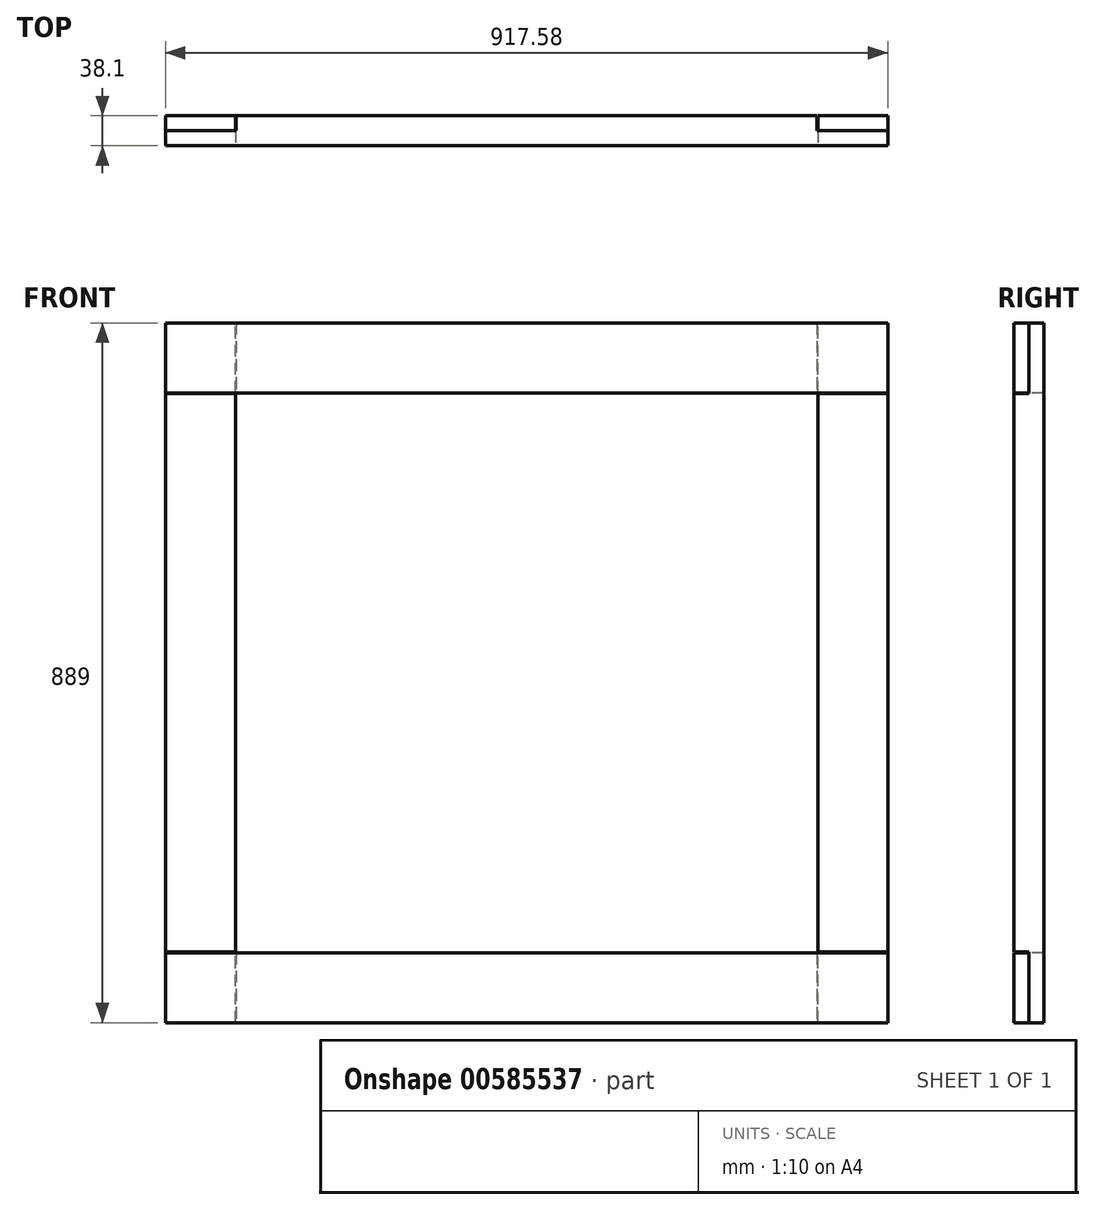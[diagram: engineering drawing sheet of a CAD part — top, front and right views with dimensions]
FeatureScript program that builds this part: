
annotation { "Feature Type Name" : "Feature", "Feature Type Description" : "" }
export const myFeature = defineFeature(function(context is Context, id is Id, definition is map)
    precondition{}
    {
        {
            var Q0;
            Q0=qCreatedBy(makeId("Front.planeOp"),FACE);
            var sketch = newSketch(context, id + "F0", { "sketchPlane" : qUnion([Q0])});
            skLineSegment(sketch, "E0.bottom", {"start": v(0, 0) * mm, "end": v(88.9, 0) * mm});
            skLineSegment(sketch, "E0.top", {"start": v(0, 889) * mm, "end": v(88.9, 889) * mm});
            skLineSegment(sketch, "E0.left", {"start": v(0, 0) * mm, "end": v(0, 889) * mm});
            skLineSegment(sketch, "E0.right", {"start": v(88.9, 0) * mm, "end": v(88.9, 889) * mm});
            skSolve(sketch);
        }
        {
            var Q0;
            Q0 = qSketchRegion(id + "F0", true);
            extrude(context, id + "F1", {"entities" : qUnion([Q0]), "oppositeDirection" : true, "depth" : 38.1 * mm, "offsetDistance" : 25.4 * mm});
        }
        {
            var Q0;
            Q0=makeQuery(id+"F1.opExtrude","CAP_FACE",FACE,{"disambiguationData":[OSD([sQuery(id+"F0.wireOp",EDGE,"E0.bottom"),sQuery(id+"F0.wireOp",EDGE,"E0.top"),sQuery(id+"F0.wireOp",EDGE,"E0.left"),sQuery(id+"F0.wireOp",EDGE,"E0.right")])],"isStart":true});
            var sketch = newSketch(context, id + "F2", { "sketchPlane" : qUnion([Q0])});
            skLineSegment(sketch, "E1.bottom", {"start": v(0, 889) * mm, "end": v(88.9, 889) * mm});
            skLineSegment(sketch, "E1.top", {"start": v(0, 799.31) * mm, "end": v(88.9, 799.31) * mm});
            skLineSegment(sketch, "E1.left", {"start": v(0, 889) * mm, "end": v(0, 799.31) * mm});
            skLineSegment(sketch, "E1.right", {"start": v(88.9, 889) * mm, "end": v(88.9, 799.31) * mm});
            skSolve(sketch);
        }
        {
            var Q0;
            Q0 = qSketchRegion(id + "F2", true);
            extrude(context, id + "F3", {"entities" : qUnion([Q0]), "operationType" : NewBodyOperationType.REMOVE, "oppositeDirection" : true, "depth" : 19.05 * mm, "offsetDistance" : 25.4 * mm});
        }
        {
            var Q0;
            Q0=makeQuery(id+"F1.opExtrude","CAP_FACE",FACE,{"disambiguationData":[OSD([sQuery(id+"F0.wireOp",EDGE,"E0.bottom"),sQuery(id+"F0.wireOp",EDGE,"E0.top"),sQuery(id+"F0.wireOp",EDGE,"E0.left"),sQuery(id+"F0.wireOp",EDGE,"E0.right")])],"isStart":true});
            var sketch = newSketch(context, id + "F4", { "sketchPlane" : qUnion([Q0])});
            skLineSegment(sketch, "E2.bottom", {"start": v(0, 0) * mm, "end": v(88.9, 0) * mm});
            skLineSegment(sketch, "E2.top", {"start": v(0, 89.69) * mm, "end": v(88.9, 89.69) * mm});
            skLineSegment(sketch, "E2.left", {"start": v(0, 0) * mm, "end": v(0, 89.69) * mm});
            skLineSegment(sketch, "E2.right", {"start": v(88.9, 0) * mm, "end": v(88.9, 89.69) * mm});
            skSolve(sketch);
        }
        {
            var Q0;
            Q0 = qSketchRegion(id + "F4", true);
            extrude(context, id + "F5", {"entities" : qUnion([Q0]), "operationType" : NewBodyOperationType.REMOVE, "oppositeDirection" : true, "depth" : 19.05 * mm, "offsetDistance" : 25.4 * mm});
        }
        {
            var Q0;
            Q0=qCreatedBy(makeId("Front.planeOp"),FACE);
            var sketch = newSketch(context, id + "F6", { "sketchPlane" : qUnion([Q0])});
            skLineSegment(sketch, "E3.bottom", {"start": v(828.68, 0) * mm, "end": v(917.58, 0) * mm});
            skLineSegment(sketch, "E3.top", {"start": v(828.68, 889) * mm, "end": v(917.58, 889) * mm});
            skLineSegment(sketch, "E3.left", {"start": v(828.68, 0) * mm, "end": v(828.68, 889) * mm});
            skLineSegment(sketch, "E3.right", {"start": v(917.58, 0) * mm, "end": v(917.58, 889) * mm});
            skSolve(sketch);
        }
        {
            var Q0;
            Q0 = qSketchRegion(id + "F6", true);
            extrude(context, id + "F7", {"entities" : qUnion([Q0]), "oppositeDirection" : true, "depth" : 38.1 * mm, "offsetDistance" : 25.4 * mm});
        }
        {
            var Q0;
            Q0=makeQuery(id+"F7.opExtrude","CAP_FACE",FACE,{"disambiguationData":[OSD([sQuery(id+"F6.wireOp",EDGE,"E3.bottom"),sQuery(id+"F6.wireOp",EDGE,"E3.top"),sQuery(id+"F6.wireOp",EDGE,"E3.left"),sQuery(id+"F6.wireOp",EDGE,"E3.right")])],"isStart":true});
            var sketch = newSketch(context, id + "F8", { "sketchPlane" : qUnion([Q0])});
            skLineSegment(sketch, "E4.bottom", {"start": v(828.68, 889) * mm, "end": v(917.58, 889) * mm});
            skLineSegment(sketch, "E4.top", {"start": v(828.68, 799.31) * mm, "end": v(917.58, 799.31) * mm});
            skLineSegment(sketch, "E4.left", {"start": v(828.68, 889) * mm, "end": v(828.68, 799.31) * mm});
            skLineSegment(sketch, "E4.right", {"start": v(917.58, 889) * mm, "end": v(917.58, 799.31) * mm});
            skLineSegment(sketch, "E5.bottom", {"start": v(917.58, 0) * mm, "end": v(828.68, 0) * mm});
            skLineSegment(sketch, "E5.top", {"start": v(917.58, 89.69) * mm, "end": v(828.68, 89.69) * mm});
            skLineSegment(sketch, "E5.left", {"start": v(917.58, 0) * mm, "end": v(917.58, 89.69) * mm});
            skLineSegment(sketch, "E5.right", {"start": v(828.68, 0) * mm, "end": v(828.68, 89.69) * mm});
            skSolve(sketch);
        }
        {
            var Q0;
            Q0 = qSketchRegion(id + "F8", true);
            extrude(context, id + "F9", {"entities" : qUnion([Q0]), "operationType" : NewBodyOperationType.REMOVE, "oppositeDirection" : true, "depth" : 19.05 * mm, "offsetDistance" : 25.4 * mm});
        }
        {
            var Q0;
            Q0=qCreatedBy(makeId("Front.planeOp"),FACE);
            var sketch = newSketch(context, id + "F10", { "sketchPlane" : qUnion([Q0])});
            skLineSegment(sketch, "E6.bottom", {"start": v(0, 889) * mm, "end": v(917.58, 889) * mm});
            skLineSegment(sketch, "E6.top", {"start": v(0, 800.1) * mm, "end": v(917.58, 800.1) * mm});
            skLineSegment(sketch, "E6.left", {"start": v(0, 889) * mm, "end": v(0, 800.1) * mm});
            skLineSegment(sketch, "E6.right", {"start": v(917.58, 889) * mm, "end": v(917.58, 800.1) * mm});
            skSolve(sketch);
        }
        {
            var Q0;
            Q0 = qSketchRegion(id + "F10", true);
            extrude(context, id + "F11", {"entities" : qUnion([Q0]), "oppositeDirection" : true, "depth" : 19.05 * mm, "offsetDistance" : 25.4 * mm});
        }
        {
            var Q0;
            Q0=makeQuery(id+"F11.opExtrude","CAP_FACE",FACE,{"disambiguationData":[OSD([sQuery(id+"F10.wireOp",EDGE,"E6.bottom"),sQuery(id+"F10.wireOp",EDGE,"E6.top"),sQuery(id+"F10.wireOp",EDGE,"E6.left"),sQuery(id+"F10.wireOp",EDGE,"E6.right")])],"isStart":false});
            var sketch = newSketch(context, id + "F12", { "sketchPlane" : qUnion([Q0])});
            skLineSegment(sketch, "E7.bottom", {"start": v(-827.89, 889) * mm, "end": v(-89.69, 889) * mm});
            skLineSegment(sketch, "E7.top", {"start": v(-827.89, 800.1) * mm, "end": v(-89.69, 800.1) * mm});
            skLineSegment(sketch, "E7.left", {"start": v(-827.89, 889) * mm, "end": v(-827.89, 800.1) * mm});
            skLineSegment(sketch, "E7.right", {"start": v(-89.69, 889) * mm, "end": v(-89.69, 800.1) * mm});
            skSolve(sketch);
        }
        {
            var Q0;
            Q0 = qSketchRegion(id + "F12", true);
            extrude(context, id + "F13", {"entities" : qUnion([Q0]), "operationType" : NewBodyOperationType.ADD, "depth" : 19.05 * mm, "offsetDistance" : 25.4 * mm});
        }
        {
            var Q0;
            Q0=qCreatedBy(makeId("Front.planeOp"),FACE);
            var sketch = newSketch(context, id + "F14", { "sketchPlane" : qUnion([Q0])});
            skLineSegment(sketch, "E8.bottom", {"start": v(0, 0) * mm, "end": v(917.58, 0) * mm});
            skLineSegment(sketch, "E8.top", {"start": v(0, 88.9) * mm, "end": v(917.58, 88.9) * mm});
            skLineSegment(sketch, "E8.left", {"start": v(0, 0) * mm, "end": v(0, 88.9) * mm});
            skLineSegment(sketch, "E8.right", {"start": v(917.58, 0) * mm, "end": v(917.58, 88.9) * mm});
            skSolve(sketch);
        }
        {
            var Q0;
            Q0 = qSketchRegion(id + "F14", true);
            extrude(context, id + "F15", {"entities" : qUnion([Q0]), "oppositeDirection" : true, "depth" : 19.05 * mm, "offsetDistance" : 25.4 * mm});
        }
        {
            var Q0;
            Q0=makeQuery(id+"F15.opExtrude","CAP_FACE",FACE,{"disambiguationData":[OSD([sQuery(id+"F14.wireOp",EDGE,"E8.bottom"),sQuery(id+"F14.wireOp",EDGE,"E8.top"),sQuery(id+"F14.wireOp",EDGE,"E8.left"),sQuery(id+"F14.wireOp",EDGE,"E8.right")])],"isStart":false});
            var sketch = newSketch(context, id + "F16", { "sketchPlane" : qUnion([Q0])});
            skLineSegment(sketch, "E9.bottom", {"start": v(-827.89, 88.9) * mm, "end": v(-89.69, 88.9) * mm});
            skLineSegment(sketch, "E9.top", {"start": v(-827.89, 0) * mm, "end": v(-89.69, 0) * mm});
            skLineSegment(sketch, "E9.left", {"start": v(-827.89, 88.9) * mm, "end": v(-827.89, 0) * mm});
            skLineSegment(sketch, "E9.right", {"start": v(-89.69, 88.9) * mm, "end": v(-89.69, 0) * mm});
            skSolve(sketch);
        }
        {
            var Q0;
            Q0 = qSketchRegion(id + "F16", true);
            extrude(context, id + "F17", {"entities" : qUnion([Q0]), "operationType" : NewBodyOperationType.ADD, "depth" : 19.05 * mm, "offsetDistance" : 25.4 * mm});
        }
    });
